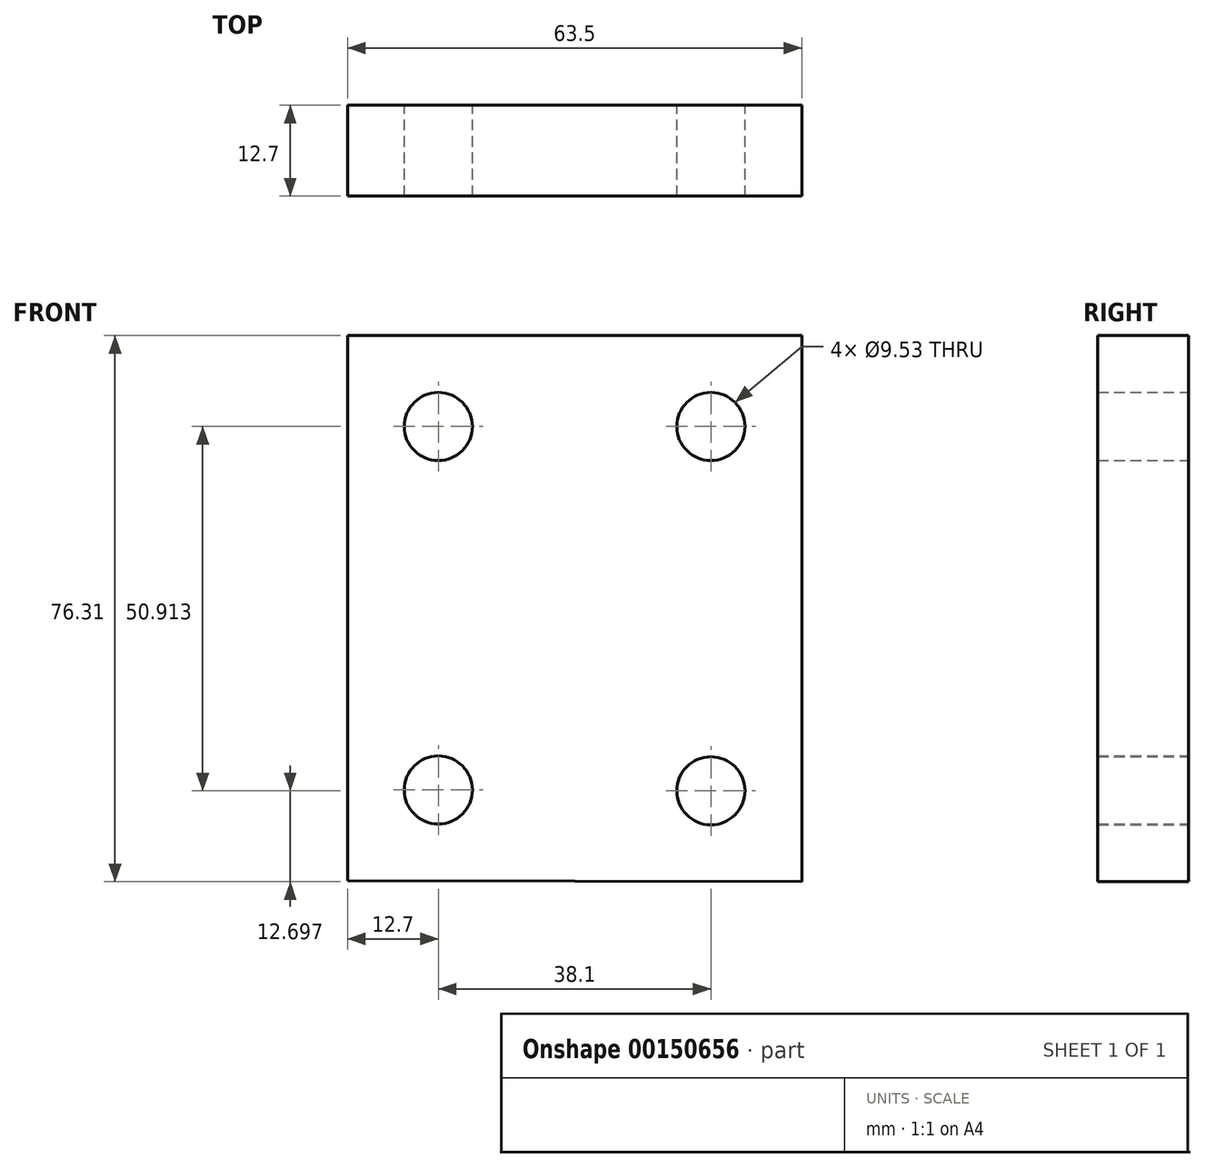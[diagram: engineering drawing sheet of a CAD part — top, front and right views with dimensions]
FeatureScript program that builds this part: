
annotation { "Feature Type Name" : "Feature", "Feature Type Description" : "" }
export const myFeature = defineFeature(function(context is Context, id is Id, definition is map)
    precondition{}
    {
        {
            var Q0;
            Q0=qCreatedBy(makeId("Front.planeOp"),FACE);
            var sketch = newSketch(context, id + "F0", { "sketchPlane" : qUnion([Q0])});
            skCircle(sketch, "E0", {"center": v(0, 0) * mm, "radius": 4.76 * mm});
            skCircle(sketch, "E1", {"center": v(38.1, -0.11) * mm, "radius": 4.76 * mm});
            skCircle(sketch, "E2", {"center": v(0, 50.8) * mm, "radius": 4.76 * mm});
            skCircle(sketch, "E3", {"center": v(38.1, 50.8) * mm, "radius": 4.76 * mm});
            skLineSegment(sketch, "E4", {"start": v(50.8, -12.81) * mm, "end": v(50.8, 63.5) * mm});
            skLineSegment(sketch, "E5", {"start": v(-12.7, -12.7) * mm, "end": v(50.8, -12.81) * mm});
            skLineSegment(sketch, "E6", {"start": v(-12.7, -12.7) * mm, "end": v(-12.7, 63.5) * mm});
            skLineSegment(sketch, "E7", {"start": v(-12.7, 63.5) * mm, "end": v(50.8, 63.5) * mm});
            skSolve(sketch);
        }
        {
            var Q0;
            Q0=makeQuery(id+"F0.imprint","IMPRINT",FACE,{"disambiguationData":[TD([[makeQuery(id+"F0.imprint","IMPRINT",EDGE,{"derivedFrom":sQuery(id+"F0.wireOp",EDGE,"E0")}),-1.0]])]});
            extrude(context, id + "F1", {"entities" : qUnion([Q0]), "depth" : 12.7 * mm});
        }
    });
